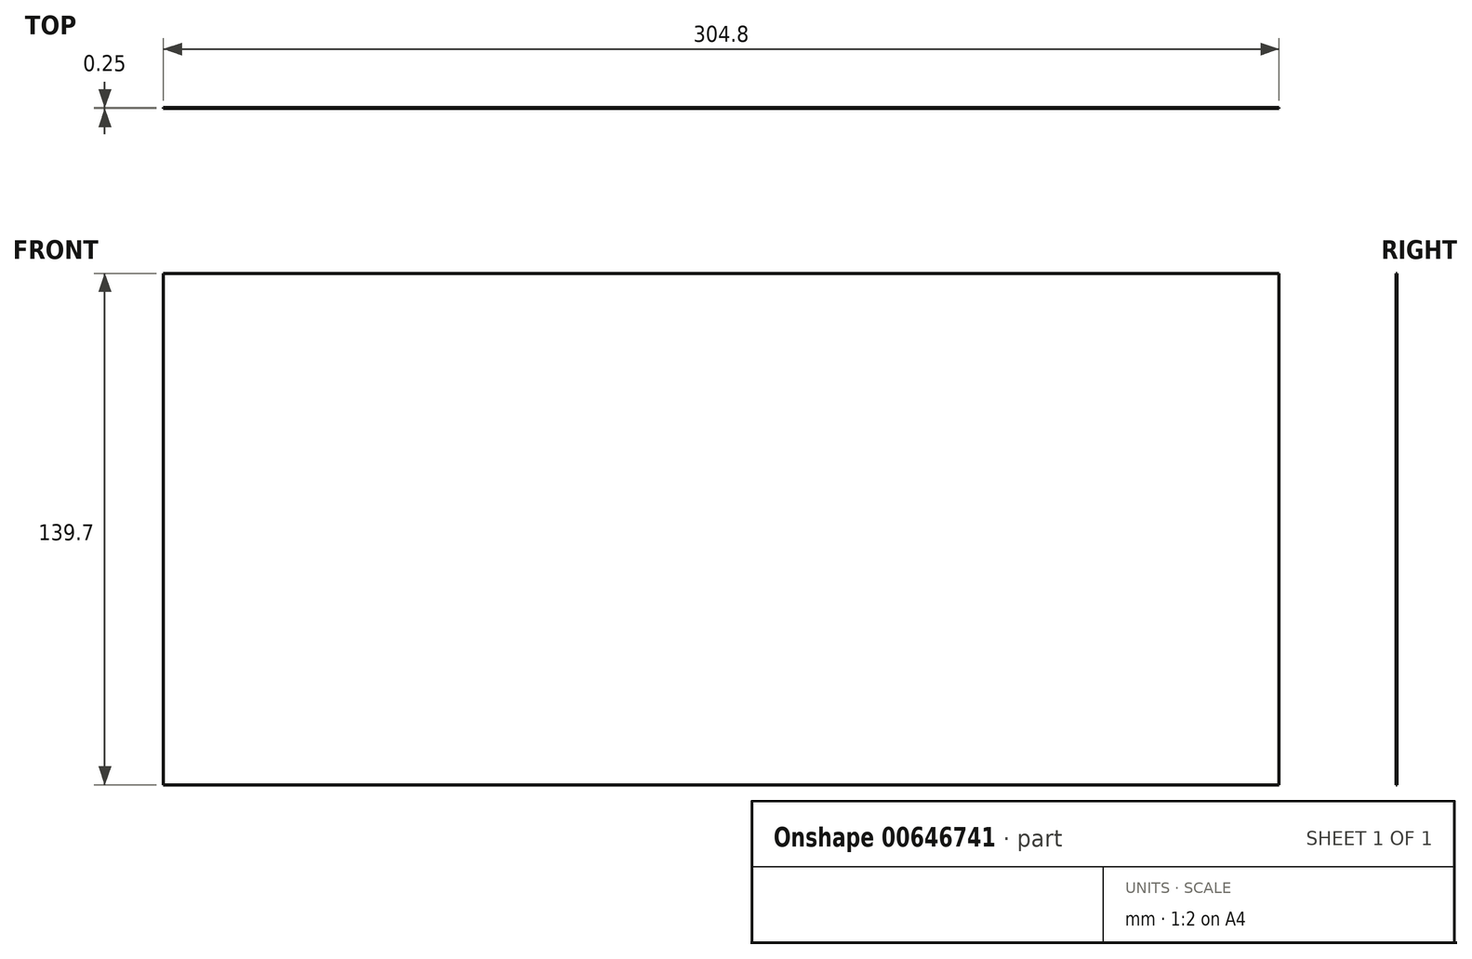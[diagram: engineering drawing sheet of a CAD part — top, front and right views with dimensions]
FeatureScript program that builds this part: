
annotation { "Feature Type Name" : "Feature", "Feature Type Description" : "" }
export const myFeature = defineFeature(function(context is Context, id is Id, definition is map)
    precondition{}
    {
        {
            var Q0;
            Q0=qCreatedBy(makeId("Front.planeOp"),FACE);
            var sketch = newSketch(context, id + "F0", { "sketchPlane" : qUnion([Q0])});
            skLineSegment(sketch, "E0.bottom", {"start": v(152.4, -69.85) * mm, "end": v(-152.4, -69.85) * mm});
            skLineSegment(sketch, "E0.top", {"start": v(152.4, 69.85) * mm, "end": v(-152.4, 69.85) * mm});
            skLineSegment(sketch, "E0.left", {"start": v(152.4, -69.85) * mm, "end": v(152.4, 69.85) * mm});
            skLineSegment(sketch, "E0.right", {"start": v(-152.4, -69.85) * mm, "end": v(-152.4, 69.85) * mm});
            skPoint(sketch, "E0.middle", {"position": v(0, 0) * mm});
            skSolve(sketch);
        }
        {
            var Q0;
            Q0=makeQuery(id+"F0.imprint","IMPRINT",FACE,{"disambiguationData":[TD([[makeQuery(id+"F0.imprint","IMPRINT",EDGE,{"derivedFrom":sQuery(id+"F0.wireOp",EDGE,"E0.bottom")}),-1.0]])]});
            extrude(context, id + "F1", {"entities" : qUnion([Q0]), "depth" : 0.25 * mm, "offsetDistance" : 25.4 * mm});
        }
    });
